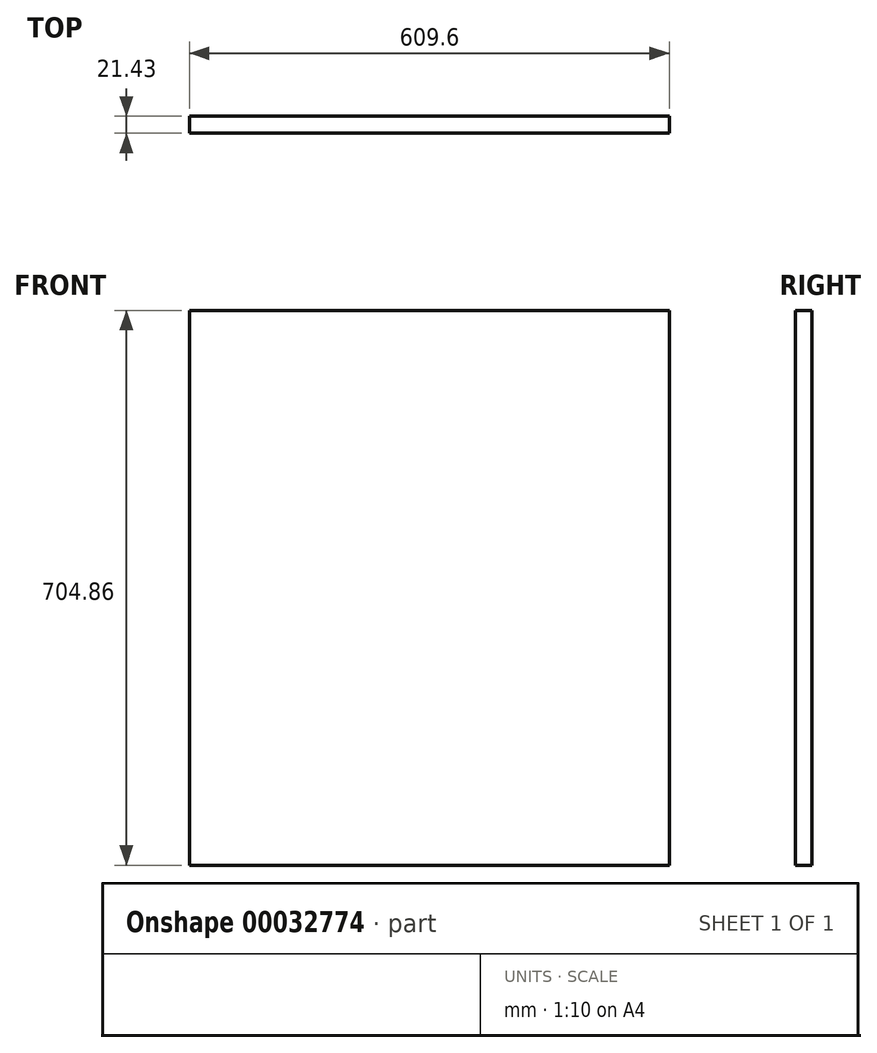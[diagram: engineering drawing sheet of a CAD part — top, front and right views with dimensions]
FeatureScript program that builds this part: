
annotation { "Feature Type Name" : "Feature", "Feature Type Description" : "" }
export const myFeature = defineFeature(function(context is Context, id is Id, definition is map)
    precondition{}
    {
        {
            var Q0;
            Q0=qCreatedBy(makeId("Front.planeOp"),FACE);
            var sketch = newSketch(context, id + "F0", { "sketchPlane" : qUnion([Q0])});
            skLineSegment(sketch, "E0.bottom", {"start": v(-304.8, 352.43) * mm, "end": v(304.8, 352.43) * mm});
            skLineSegment(sketch, "E0.top", {"start": v(-304.8, -352.43) * mm, "end": v(304.8, -352.43) * mm});
            skLineSegment(sketch, "E0.left", {"start": v(-304.8, 352.43) * mm, "end": v(-304.8, -352.43) * mm});
            skLineSegment(sketch, "E0.right", {"start": v(304.8, 352.43) * mm, "end": v(304.8, -352.43) * mm});
            skLineSegment(sketch, "E1", {"start": v(0, -352.43) * mm, "end": v(0, 352.43) * mm, "construction": true});
            skSolve(sketch);
        }
        {
            var Q0;
            Q0=qSketchRegion(id+"F0",true);
            extrude(context, id + "F1", {"entities" : qUnion([Q0]), "depth" : 21.43 * mm});
        }
    });
